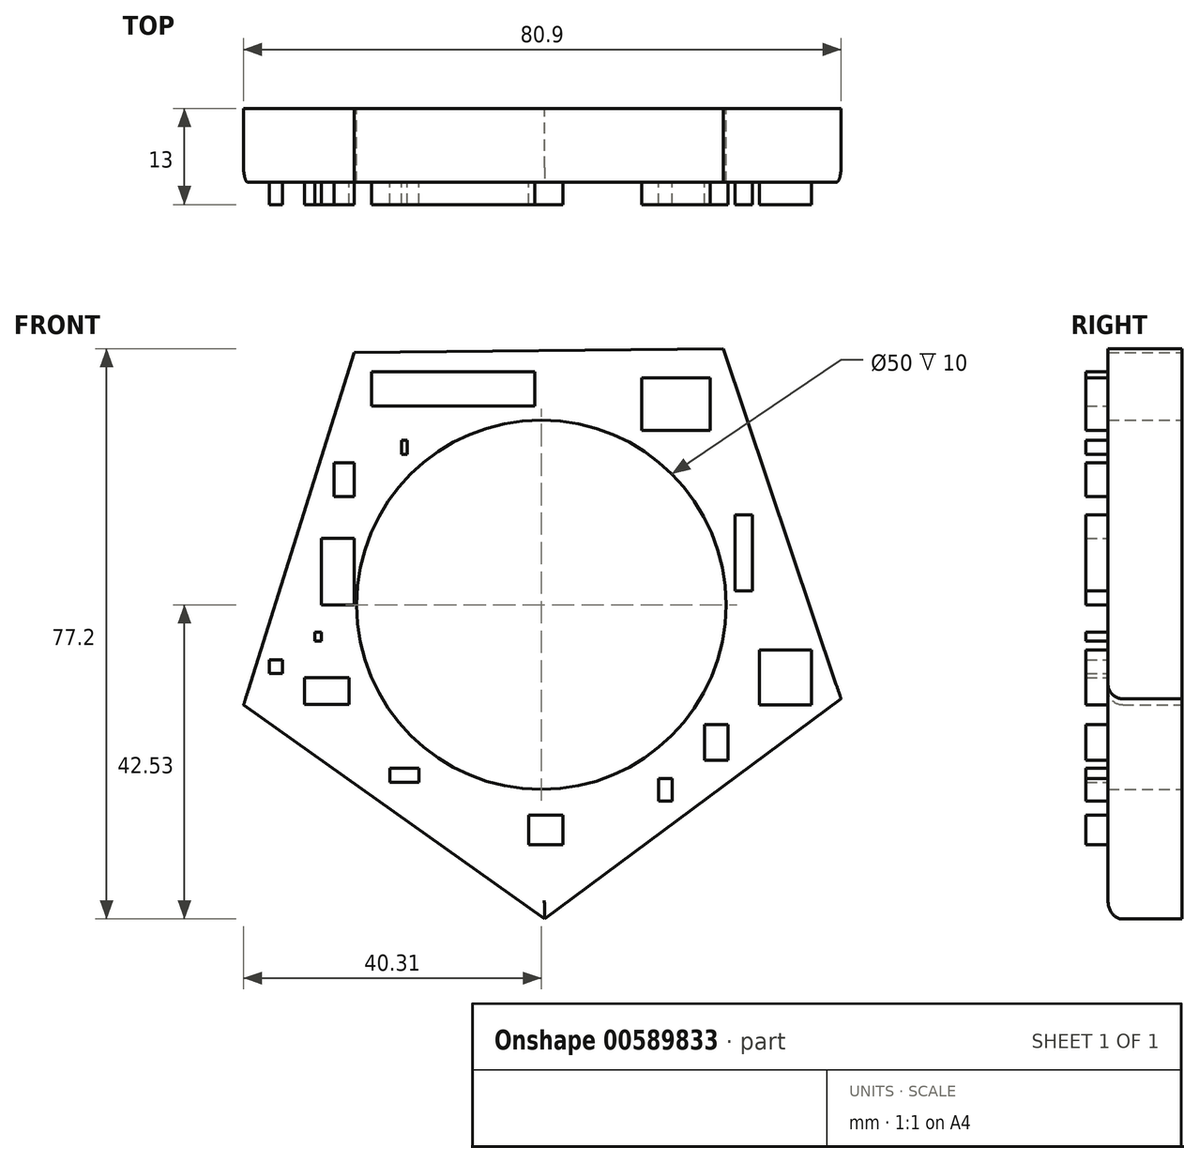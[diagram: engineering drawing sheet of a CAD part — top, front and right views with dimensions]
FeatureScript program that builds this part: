
annotation { "Feature Type Name" : "Feature", "Feature Type Description" : "" }
export const myFeature = defineFeature(function(context is Context, id is Id, definition is map)
    precondition{}
    {
        {
            var Q0;
            Q0=qCreatedBy(makeId("Front.planeOp"),FACE);
            var sketch = newSketch(context, id + "F0", { "sketchPlane" : qUnion([Q0])});
            skCircle(sketch, "E0.cCircle", {"center": v(0, 0) * mm, "radius": 34.4 * mm, "construction": true});
            skLineSegment(sketch, "E0.0", {"start": v(-40.31, -13.56) * mm, "end": v(-25.36, 34.15) * mm});
            skLineSegment(sketch, "E0.1", {"start": v(-25.36, 34.15) * mm, "end": v(24.64, 34.67) * mm});
            skLineSegment(sketch, "E0.2", {"start": v(24.64, 34.67) * mm, "end": v(40.59, -12.72) * mm});
            skLineSegment(sketch, "E0.3", {"start": v(40.59, -12.72) * mm, "end": v(0.44, -42.53) * mm});
            skLineSegment(sketch, "E0.4", {"start": v(0.44, -42.53) * mm, "end": v(-40.31, -13.56) * mm});
            skPoint(sketch, "E0.0.midPoint", {"position": v(-32.83, 10.3) * mm});
            skCircle(sketch, "E1", {"center": v(0, 0) * mm, "radius": 25 * mm});
            skSolve(sketch);
        }
        {
            var Q0;
            Q0 = qSketchRegion(id + "F0", true);
            extrude(context, id + "F1", {"entities" : qUnion([Q0]), "depth" : 10 * mm, "offsetDistance" : 25 * mm});
        }
        {
            var Q0;
            Q0=makeQuery(id+"F1.opExtrude","CAP_FACE",FACE,{"disambiguationData":[OSD([sQuery(id+"F0.wireOp",EDGE,"E0.0"),sQuery(id+"F0.wireOp",EDGE,"E0.1"),sQuery(id+"F0.wireOp",EDGE,"E0.2"),sQuery(id+"F0.wireOp",EDGE,"E0.3"),sQuery(id+"F0.wireOp",EDGE,"E0.4"),sQuery(id+"F0.wireOp",EDGE,"E1")])],"isStart":false});
            var sketch = newSketch(context, id + "F2", { "sketchPlane" : qUnion([Q0])});
            skLineSegment(sketch, "E2.bottom", {"start": v(-30.7, -4.94) * mm, "end": v(-29.75, -4.94) * mm});
            skLineSegment(sketch, "E2.top", {"start": v(-30.7, -3.68) * mm, "end": v(-29.75, -3.68) * mm});
            skLineSegment(sketch, "E2.left", {"start": v(-30.7, -4.94) * mm, "end": v(-30.7, -3.68) * mm});
            skLineSegment(sketch, "E2.right", {"start": v(-29.75, -4.94) * mm, "end": v(-29.75, -3.68) * mm});
            skLineSegment(sketch, "E3.bottom", {"start": v(-32.07, -13.48) * mm, "end": v(-26.06, -13.48) * mm});
            skLineSegment(sketch, "E3.top", {"start": v(-32.07, -9.9) * mm, "end": v(-26.06, -9.9) * mm});
            skLineSegment(sketch, "E3.left", {"start": v(-32.07, -13.48) * mm, "end": v(-32.07, -9.9) * mm});
            skLineSegment(sketch, "E3.right", {"start": v(-26.06, -13.48) * mm, "end": v(-26.06, -9.9) * mm});
            skLineSegment(sketch, "E4.bottom", {"start": v(-20.47, -22.13) * mm, "end": v(-16.57, -22.13) * mm});
            skLineSegment(sketch, "E4.top", {"start": v(-20.47, -24.02) * mm, "end": v(-16.57, -24.02) * mm});
            skLineSegment(sketch, "E4.left", {"start": v(-20.47, -22.13) * mm, "end": v(-20.47, -24.02) * mm});
            skLineSegment(sketch, "E4.right", {"start": v(-16.57, -22.13) * mm, "end": v(-16.57, -24.02) * mm});
            skLineSegment(sketch, "E5.bottom", {"start": v(-1.7, -32.46) * mm, "end": v(2.94, -32.46) * mm});
            skLineSegment(sketch, "E5.top", {"start": v(-1.7, -28.45) * mm, "end": v(2.94, -28.45) * mm});
            skLineSegment(sketch, "E5.left", {"start": v(-1.7, -32.46) * mm, "end": v(-1.7, -28.45) * mm});
            skLineSegment(sketch, "E5.right", {"start": v(2.94, -32.46) * mm, "end": v(2.94, -28.45) * mm});
            skLineSegment(sketch, "E6.bottom", {"start": v(15.9, -23.5) * mm, "end": v(17.7, -23.5) * mm});
            skLineSegment(sketch, "E6.top", {"start": v(15.9, -26.56) * mm, "end": v(17.7, -26.56) * mm});
            skLineSegment(sketch, "E6.left", {"start": v(15.9, -23.5) * mm, "end": v(15.9, -26.56) * mm});
            skLineSegment(sketch, "E6.right", {"start": v(17.7, -23.5) * mm, "end": v(17.7, -26.56) * mm});
            skLineSegment(sketch, "E7.bottom", {"start": v(29.5, -13.56) * mm, "end": v(36.57, -13.56) * mm});
            skLineSegment(sketch, "E7.top", {"start": v(29.5, -6.1) * mm, "end": v(36.57, -6.1) * mm});
            skLineSegment(sketch, "E7.left", {"start": v(29.5, -13.56) * mm, "end": v(29.5, -6.1) * mm});
            skLineSegment(sketch, "E7.right", {"start": v(36.57, -13.56) * mm, "end": v(36.57, -6.1) * mm});
            skLineSegment(sketch, "E8.bottom", {"start": v(25.29, -16.22) * mm, "end": v(22.12, -16.22) * mm});
            skLineSegment(sketch, "E8.top", {"start": v(25.29, -21.07) * mm, "end": v(22.12, -21.07) * mm});
            skLineSegment(sketch, "E8.left", {"start": v(25.29, -16.22) * mm, "end": v(25.29, -21.07) * mm});
            skLineSegment(sketch, "E8.right", {"start": v(22.12, -16.22) * mm, "end": v(22.12, -21.07) * mm});
            skLineSegment(sketch, "E9.bottom", {"start": v(28.55, 12.14) * mm, "end": v(26.24, 12.14) * mm});
            skLineSegment(sketch, "E9.top", {"start": v(28.55, 1.91) * mm, "end": v(26.24, 1.91) * mm});
            skLineSegment(sketch, "E9.left", {"start": v(28.55, 12.14) * mm, "end": v(28.55, 1.91) * mm});
            skLineSegment(sketch, "E9.right", {"start": v(26.24, 12.14) * mm, "end": v(26.24, 1.91) * mm});
            skLineSegment(sketch, "E10.bottom", {"start": v(22.86, 23.63) * mm, "end": v(13.58, 23.63) * mm});
            skLineSegment(sketch, "E10.top", {"start": v(22.86, 30.7) * mm, "end": v(13.58, 30.7) * mm});
            skLineSegment(sketch, "E10.left", {"start": v(22.86, 23.63) * mm, "end": v(22.86, 30.7) * mm});
            skLineSegment(sketch, "E10.right", {"start": v(13.58, 23.63) * mm, "end": v(13.58, 30.7) * mm});
            skLineSegment(sketch, "E11.bottom", {"start": v(-0.86, 31.54) * mm, "end": v(-23, 31.54) * mm});
            skLineSegment(sketch, "E11.top", {"start": v(-0.86, 26.9) * mm, "end": v(-23, 26.9) * mm});
            skLineSegment(sketch, "E11.left", {"start": v(-0.86, 31.54) * mm, "end": v(-0.86, 26.9) * mm});
            skLineSegment(sketch, "E11.right", {"start": v(-23, 31.54) * mm, "end": v(-23, 26.9) * mm});
            skLineSegment(sketch, "E12.bottom", {"start": v(-25.36, 19.2) * mm, "end": v(-28.06, 19.2) * mm});
            skLineSegment(sketch, "E12.top", {"start": v(-25.36, 14.67) * mm, "end": v(-28.06, 14.67) * mm});
            skLineSegment(sketch, "E12.left", {"start": v(-25.36, 19.2) * mm, "end": v(-25.36, 14.67) * mm});
            skLineSegment(sketch, "E12.right", {"start": v(-28.06, 19.2) * mm, "end": v(-28.06, 14.67) * mm});
            skLineSegment(sketch, "E13.bottom", {"start": v(-18.15, 22.26) * mm, "end": v(-18.89, 22.26) * mm});
            skLineSegment(sketch, "E13.top", {"start": v(-18.15, 20.36) * mm, "end": v(-18.89, 20.36) * mm});
            skLineSegment(sketch, "E13.left", {"start": v(-18.15, 22.26) * mm, "end": v(-18.15, 20.36) * mm});
            skLineSegment(sketch, "E13.right", {"start": v(-18.89, 22.26) * mm, "end": v(-18.89, 20.36) * mm});
            skLineSegment(sketch, "E14.bottom", {"start": v(-29.75, 8.97) * mm, "end": v(-25.36, 8.97) * mm});
            skLineSegment(sketch, "E14.top", {"start": v(-29.75, 0) * mm, "end": v(-25.36, 0) * mm});
            skLineSegment(sketch, "E14.left", {"start": v(-29.75, 8.97) * mm, "end": v(-29.75, 0) * mm});
            skLineSegment(sketch, "E14.right", {"start": v(-25.36, 8.97) * mm, "end": v(-25.36, 0) * mm});
            skLineSegment(sketch, "E15.bottom", {"start": v(-36.81, -7.47) * mm, "end": v(-35.02, -7.47) * mm});
            skLineSegment(sketch, "E15.top", {"start": v(-36.81, -9.27) * mm, "end": v(-35.02, -9.27) * mm});
            skLineSegment(sketch, "E15.left", {"start": v(-36.81, -7.47) * mm, "end": v(-36.81, -9.27) * mm});
            skLineSegment(sketch, "E15.right", {"start": v(-35.02, -7.47) * mm, "end": v(-35.02, -9.27) * mm});
            skSolve(sketch);
        }
        {
            var Q0;
            Q0 = qSketchRegion(id + "F2", true);
            extrude(context, id + "F3", {"entities" : qUnion([Q0]), "operationType" : NewBodyOperationType.ADD, "depth" : 3 * mm, "offsetDistance" : 25 * mm});
        }
        {
            var Q0;
            Q0=makeQuery(id+"F1.opExtrude","CAP_EDGE",EDGE,{"disambiguationData":[OSD([sQuery(id+"F0.wireOp",EDGE,"E0.4")])],"isStart":false});
            var Q1;
            Q1=makeQuery(id+"F1.opExtrude","CAP_EDGE",EDGE,{"disambiguationData":[OSD([sQuery(id+"F0.wireOp",EDGE,"E0.3")])],"isStart":false});
            fillet(context, id + "F4", {"entities" : qUnion([Q0, Q1]), "radius" : 2 * mm, "tangentPropagation" : true, "allowEdgeOverflow" : false});
        }
    });
